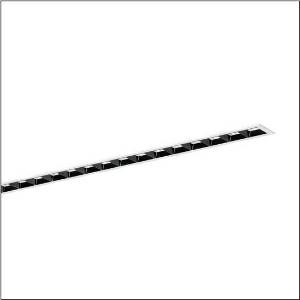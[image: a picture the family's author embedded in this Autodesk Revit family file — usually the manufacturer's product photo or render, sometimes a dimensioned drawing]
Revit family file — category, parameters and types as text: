
# Revit family: silica_r__21_51mx14db45wb_b1e5
name_source: partatom
category: Lighting Fixtures
units: mm (PartAtom-declared; Revit-internal decimal feet)

## family parameters
Cut with Voids When Loaded = No
Host = Face
Light Source = No
Part Type = Normal
Room Calculation Point = No
Round Connector Dimension = Use Diameter
Shared = No

## types (1)
- --- (1 x LED, 5400 lm, 37.6 W, 4000K)
    Apparent Load = 38 VA
    CIE Flux Codes = 74 94 99 100 100
    Color Rendering = 80
    Color Temperature = 4000K
    Default Elevation = 1800 mm
    Description = Silica® 21, office luminaire, primary light control with darklight reflector, of PMMA, black, light emission: direct distribution, primary light characteristic: asymmetric, installation type: recessed, LED, rated luminous flux: 5.400lm, luminous efficacy: 144lm/W, light colour: 840, colour temperature: 4000K, with terminal, 3+2-pole, max. 2.5mm², mains connection: 220..240V, AC, 50/60Hz, rated input power: 37.6W, luminaire housing, of aluminium, traffic white (RAL 9016), length: 1.528mm, width: 79mm, height: 53mm, protection rating (complete): IP20, insulation class (complete): insulation class I (protective earthing), certification: CE, permissible operating ambient temperature: 0..+35°C, standard: EN 50419, packaging unit: 1 piece
    Height = 0 mm  [stored 0 ft]
    Lamp = 1 x LED
    Lamp Light Flux = 5400 lm
    Lamp Power = 37.6 W
    Lamp count = 1
    Length = 1527 mm
    Luminous efficacy = 144 lm/W
    Manufacturer = Siteco
    ModVariant = No
    Model = 51MX14DB45WB
    Mounting Place = Ceiling
    Mounting Type = Recessed
    Number of Poles = 1
    OnlyDefault = Yes
    Power Factor = 1
    Product Name = Silica® 21
    Product group = office luminaire | ceiling recessed
    ProductGroupID = 400
    Protection Class = Protection class I
    Protection Degree = IP 20
    RLX_Detail_Level = 1
    RlxData = <blob elided: 42917 chars, md5=f94f796b>
    Socket = socket
    Standby Power = 0 W
    System Light Flux = 5400 lm
    System Power = 38 W
    Type Comments = factory setting: luminous flux: 100 % | dim-lin: 254 | 418 mA
    Type Image = l_1251632.jpg
    URL = http://relux.com
    VarID = @adj_031631
    Voltage = 0 V
    Weight = 0.00 kg
    Width = 79 mm

note: [stored X ft] marks values corroborated as IEEE doubles in the binary element streams (Revit-internal decimal feet)

## geometry (parser evidence)
native form markers: Blend x4, Sweep x9
no freeform markers — native parametric forms only
